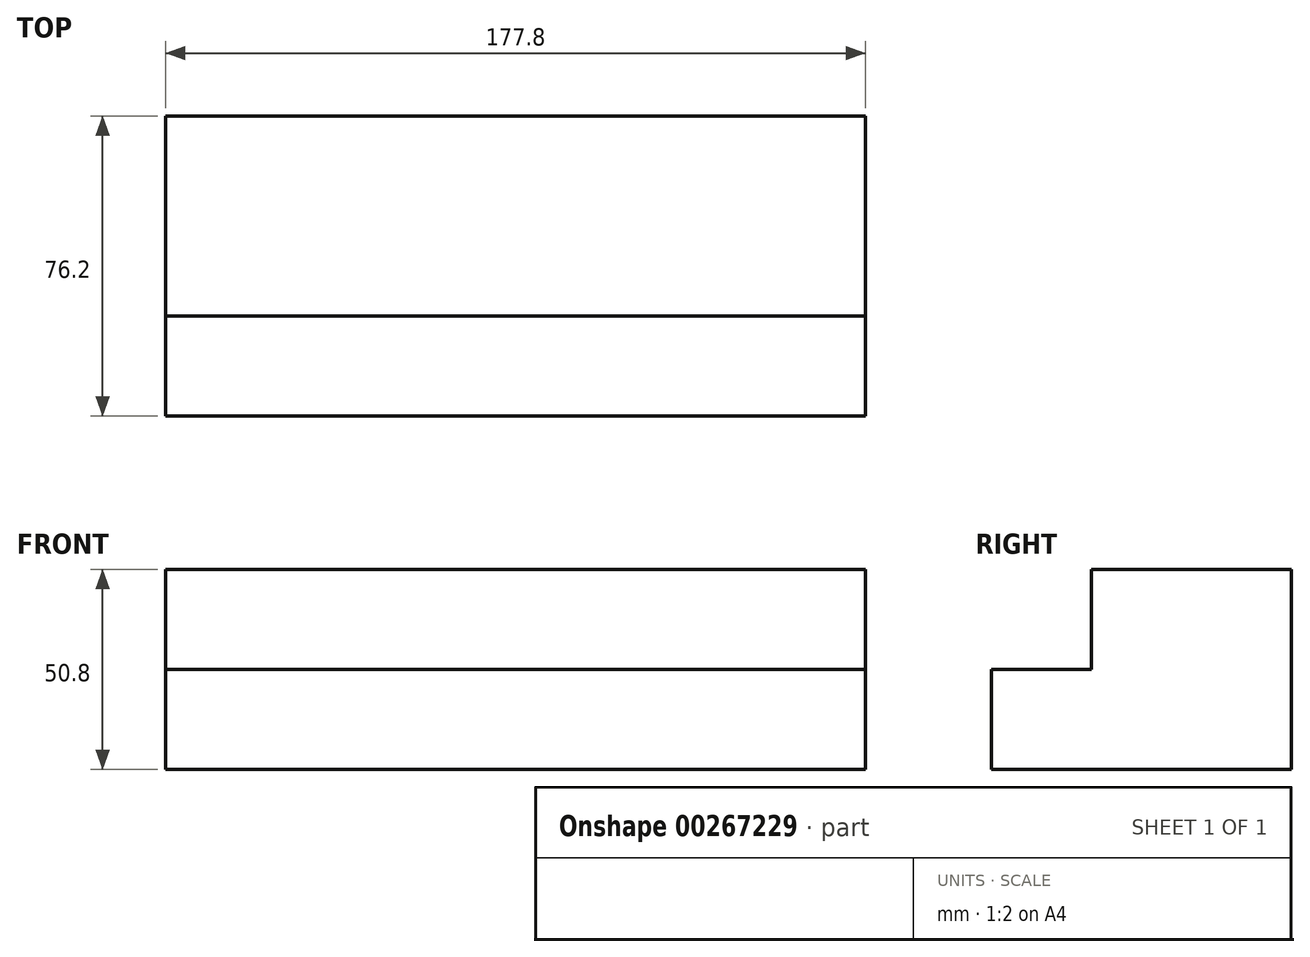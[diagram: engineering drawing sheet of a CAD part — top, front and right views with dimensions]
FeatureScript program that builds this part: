
annotation { "Feature Type Name" : "Feature", "Feature Type Description" : "" }
export const myFeature = defineFeature(function(context is Context, id is Id, definition is map)
    precondition{}
    {
        {
            var Q0;
            Q0=qCreatedBy(makeId("Right.planeOp"),FACE);
            var sketch = newSketch(context, id + "F0", { "sketchPlane" : qUnion([Q0])});
            skLineSegment(sketch, "E0.bottom", {"start": v(0.24, 0) * mm, "end": v(51.04, 0) * mm});
            skLineSegment(sketch, "E0.top", {"start": v(-25.16, -50.8) * mm, "end": v(51.04, -50.8) * mm});
            skLineSegment(sketch, "E0.left", {"start": v(-25.16, -25.4) * mm, "end": v(-25.16, -50.8) * mm});
            skLineSegment(sketch, "E0.right", {"start": v(51.04, 0) * mm, "end": v(51.04, -50.8) * mm});
            skLineSegment(sketch, "E1.top", {"start": v(-25.16, -25.4) * mm, "end": v(0.24, -25.4) * mm});
            skLineSegment(sketch, "E1.right", {"start": v(0.24, 0) * mm, "end": v(0.24, -25.4) * mm});
            skPoint(sketch, "E2.orphan", {"position": v(-25.16, 0) * mm});
            skSolve(sketch);
        }
        {
            var Q0;
            Q0 = qSketchRegion(id + "F0", true);
            extrude(context, id + "F1", {"entities" : qUnion([Q0]), "depth" : 25.4 * mm});
        }
        {
            var Q0;
            Q0=makeQuery(id+"F1.opExtrude","CAP_FACE",FACE,{"disambiguationData":[OSD([sQuery(id+"F0.wireOp",EDGE,"E0.bottom"),sQuery(id+"F0.wireOp",EDGE,"E0.top"),sQuery(id+"F0.wireOp",EDGE,"E0.left"),sQuery(id+"F0.wireOp",EDGE,"E0.right"),sQuery(id+"F0.wireOp",EDGE,"E1.top"),sQuery(id+"F0.wireOp",EDGE,"E1.right")])],"isStart":false});
            extrude(context, id + "F2", {"entities" : qUnion([Q0]), "operationType" : NewBodyOperationType.ADD, "depth" : 152.4 * mm});
        }
    });
